# Revit family: Atdec-Bracket-TH-3070-UT-
name_source: partatom
category: Generic Models
revit_build: Autodesk Revit 2016 (Build: 20150220_1215(x64)
units: mm (PartAtom-declared; Revit-internal decimal feet)

## family parameters
Can host rebar = No
Cut with Voids When Loaded = No
Host = Face
Part Type = Normal
Room Calculation Point = No
Round Connector Dimension = Use Diameter
Shared = No

## types (1)
- TH-3070-UT
    Assembly Code = E1010800
    Colour Options = Black
    Default Elevation = 1219 mm
    Description = Tilting angle wall mount
    Flat screen maximum supported weight = 91kg (200lb)
    Manufacturer = Atdec
    Master Carton Dimensions = 900mm (35.4") Lenght, 300mm (11.8") Width, 320mm (12.6") Height
    Material = Steel
    Maximum distance from wall (mm) = 72.5 (2.85")
    Minimum distance from wall (mm) = 72.5 (2.85")
    Model = TH-3070-UT
    Pan Adjustment = -
    Product Family = Wall Mount Rail
    Product Information Link = https://www.atdec.com.au
    Range of Motion = Tilt
    Security feature = Can be secured with padlock (not included)
    Single Unit Dimensions = 885mm (34.6") Lenght, 275mm (10.8") Width, 75mm (2.95") Height
    Single units per master pack = 4
    Tilt Adjustment = 15° of downward and 5° of upward tilt
    UPC Code = 881493004788
    URL = www.atdec.com.au
    Universal Height (mm) = From 125 to 500
    Universal Width (mm) = From 180 to 800
    VESA mounting hole pattern, mm = 200x200, 200x300, 200x400, 300x200, 300x300, 400x200, 400x300, 400x400, 600x200, 600x400, 800x200, 800x400
    Warranty = 10 years
    Weight, Master Carton = 28kg (61.7lb)
    Weight, Single Unit = 6.84kg (15lb)

## geometry (parser evidence)
native form markers: Sweep x4
no freeform markers — native parametric forms only
